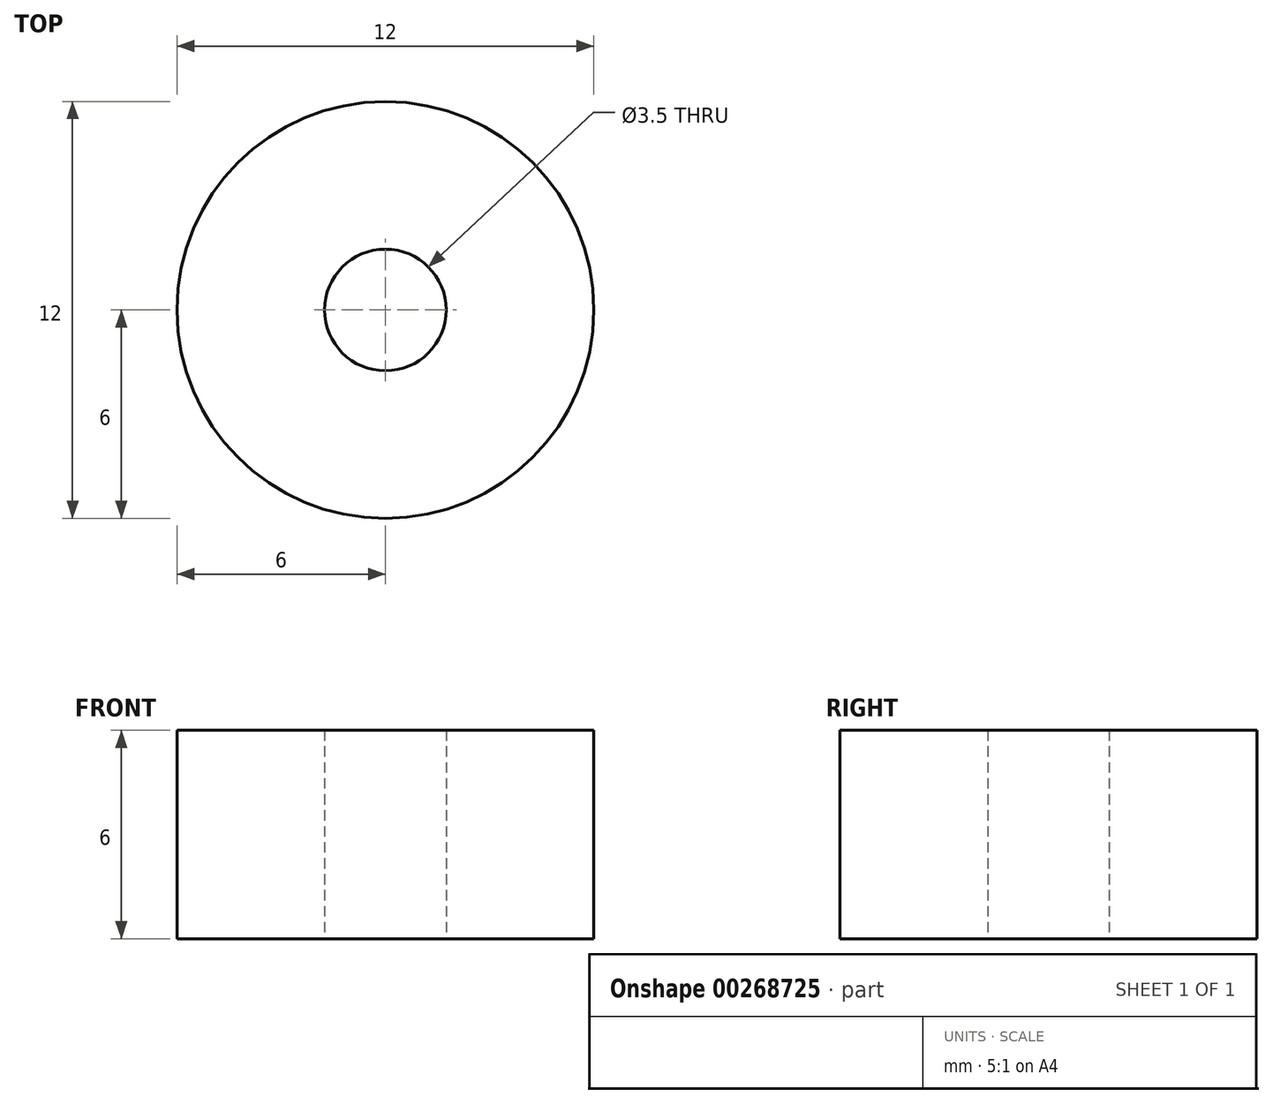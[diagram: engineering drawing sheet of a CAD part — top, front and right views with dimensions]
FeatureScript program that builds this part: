
annotation { "Feature Type Name" : "Feature", "Feature Type Description" : "" }
export const myFeature = defineFeature(function(context is Context, id is Id, definition is map)
    precondition{}
    {
        {
            var Q0;
            Q0=qCreatedBy(makeId("Top.planeOp"),FACE);
            var sketch = newSketch(context, id + "F0", { "sketchPlane" : qUnion([Q0])});
            skCircle(sketch, "E0", {"center": v(0, 0) * mm, "radius": 6 * mm});
            skCircle(sketch, "E1", {"center": v(0, 0) * mm, "radius": 1.75 * mm});
            skSolve(sketch);
        }
        {
            var Q0;
            Q0=makeQuery(id+"F0.imprint","IMPRINT",FACE,{"disambiguationData":[TD([[makeQuery(id+"F0.imprint","IMPRINT",EDGE,{"derivedFrom":sQuery(id+"F0.wireOp",EDGE,"E0")}),1.0]])]});
            extrude(context, id + "F1", {"entities" : qUnion([Q0]), "depth" : 6 * mm});
        }
    });
